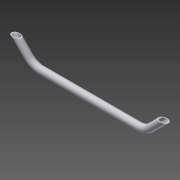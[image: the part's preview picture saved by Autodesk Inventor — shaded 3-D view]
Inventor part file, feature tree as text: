
AUTODESK INVENTOR PART (.ipt)
format: ipt  version: 2015 (Build 190159000, 159)  size: 139,776 bytes
history: native  units: mm
features: sketch x4, other x3, extrude x2, shell x1
ambient origin geometry x8: Origin, YZ Plane, XZ Plane, XY Plane, X Axis, Y Axis, Z Axis, Center Point
bodies: Body1 (feature_tree)
feature tree (10):
  other  "Bryła1"
  extrude  "Wyciągnięcie proste1"  Depth=20.0mm
  shell  "Skorupa1"  Thickness=475.0mm
  other  "Gięcie części1"
  other  "Gięcie części2"
  extrude  "Wyciągnięcie proste2"  Depth=2.0mm
  sketch  "Szkic1"
  sketch  "Szkic2"
  sketch  "Szkic3"
  sketch  "Szkic4"
